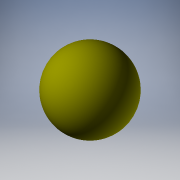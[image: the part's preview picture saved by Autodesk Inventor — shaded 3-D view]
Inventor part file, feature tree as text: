
AUTODESK INVENTOR PART (.ipt)
format: ipt  version: 2019 (Build 230136000, 136)  size: 144,896 bytes
history: native  units: mm
features: other x7, revolve x1, sketch x1
ambient origin geometry x8: Origin, YZ Plane, XZ Plane, XY Plane, X Axis, Y Axis, Z Axis, Center Point
bodies: Solid1 (feature_tree)
feature tree (9):
  revolve  "Revolution1"  [1 undecoded]
  other  "ball1_XY"
  other  "ball1_YZ"
  other  "ball1_ZX"
  other  "ball1_X"
  other  "ball1_Y"
  other  "ball1_Z"
  other  "ball1_Center"
  sketch  "Sketch_6"  dims[d0=360.0deg]
note: 1 required parameter value undecoded (feature->parameter linkage not recoverable at this tier; creation-order binding heuristic only, values carry confidence <= 0.55)
